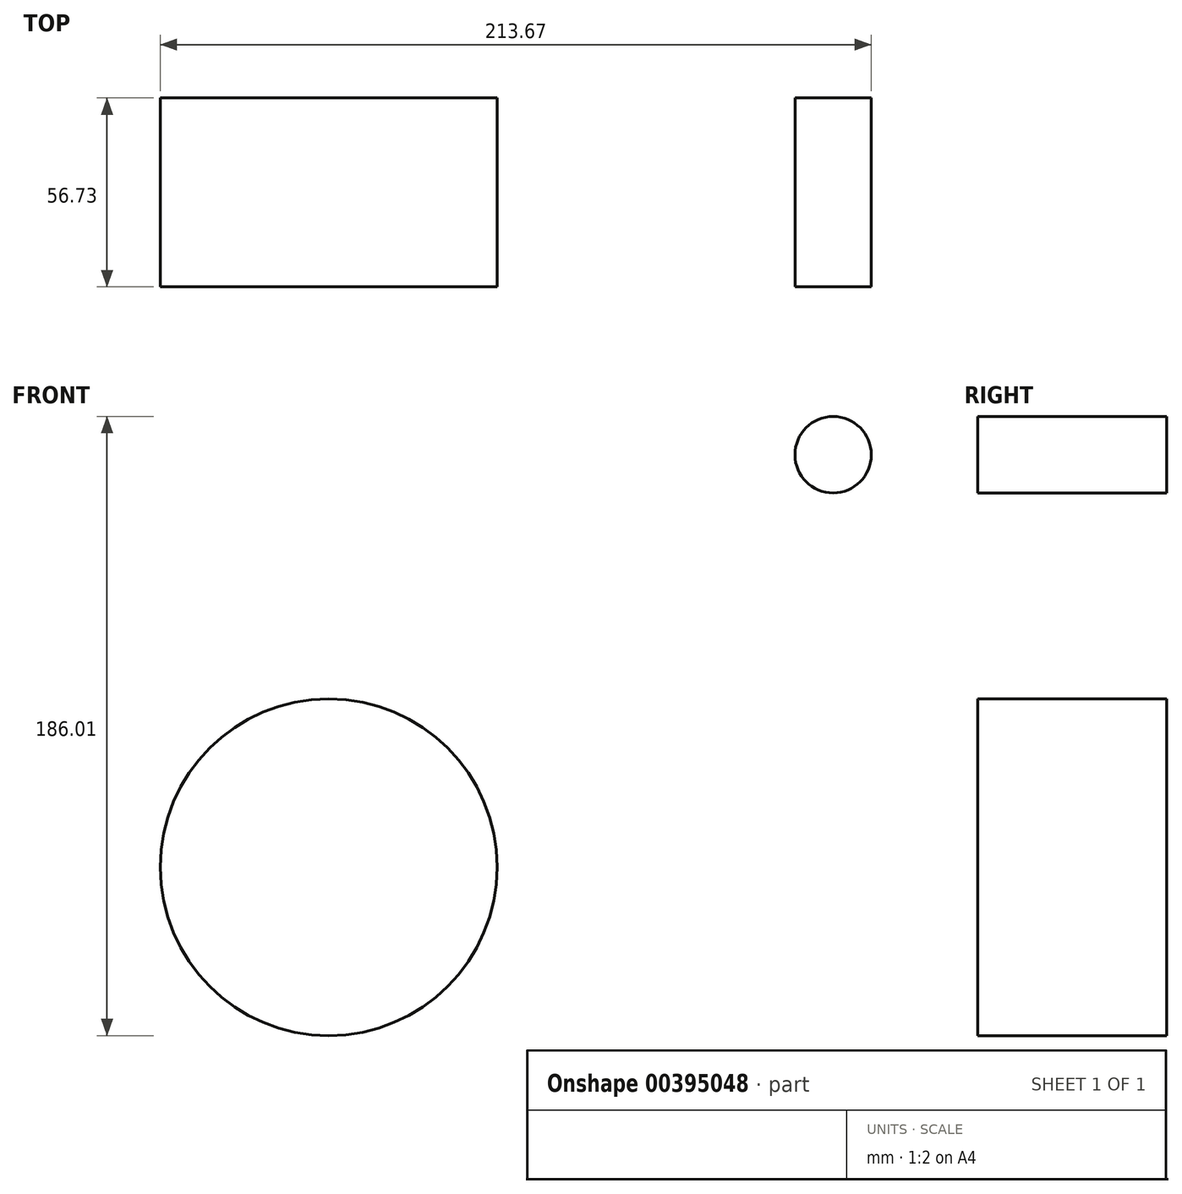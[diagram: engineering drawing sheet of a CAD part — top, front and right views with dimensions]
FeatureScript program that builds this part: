
annotation { "Feature Type Name" : "Feature", "Feature Type Description" : "" }
export const myFeature = defineFeature(function(context is Context, id is Id, definition is map)
    precondition{}
    {
        {
            var Q0;
            Q0=qCreatedBy(makeId("Front.planeOp"),FACE);
            var sketch = newSketch(context, id + "F0", { "sketchPlane" : qUnion([Q0])});
            skCircle(sketch, "E0", {"center": v(21.1, 36.28) * mm, "radius": 50.6 * mm});
            skCircle(sketch, "E1", {"center": v(172.68, 160.2) * mm, "radius": 11.48 * mm});
            skSolve(sketch);
        }
        {
            var Q0;
            Q0 = qSketchRegion(id + "F0", true);
            extrude(context, id + "F1", {"entities" : qUnion([Q0]), "depth" : 56.73 * mm});
        }
    });
